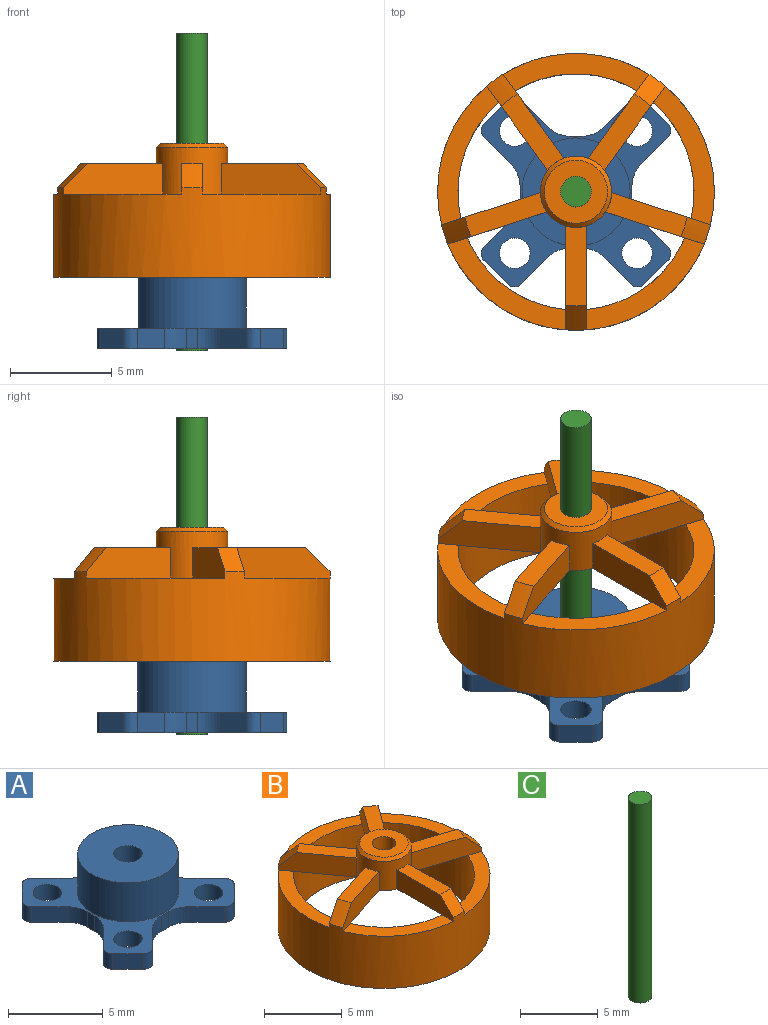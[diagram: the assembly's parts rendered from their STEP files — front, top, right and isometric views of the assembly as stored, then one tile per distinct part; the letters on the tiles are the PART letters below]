
ASSEMBLY  parts=3 mates=2
PART A: 41 faces, bbox 9.3x9.3x3.5 mm
  f0: cylinder r=1.5mm len=1.06mm, axis (0,0,-1), area 1.2mm2, adj f1,f36,f37,f38
  f1: plane 1.33x1.33mm, normal (-0.71,-0.71,0), area 1.9mm2, adj f0,f2,f37,f38
  f2: cylinder r=0.5mm len=1mm, axis (0,0,-1), area 0.8mm2, adj f1,f3,f37,f38
  f3: plane 1.13x1.13mm, normal (0.71,-0.71,0), area 1.6mm2, adj f2,f4,f37,f38
  f4: cylinder r=0.5mm len=1mm, axis (0,0,-1), area 0.8mm2, adj f3,f5,f37,f38
  f5: plane 1.33x1.33mm, normal (0.71,0.71,0), area 1.9mm2, adj f4,f6,f37,f38
  f6: cylinder r=1.5mm len=1.06mm, axis (0,0,-1), area 1.2mm2, adj f5,f7,f37,f38
  f7: plane 1x0.57mm, normal (1,0,0), area 0.6mm2, adj f6,f8,f37,f38
  f8: cylinder r=1.5mm len=1.06mm, axis (0,0,-1), area 1.2mm2, adj f7,f9,f37,f38
  f9: plane 1.33x1.33mm, normal (0.71,-0.71,0), area 1.9mm2, adj f8,f10,f37,f38
  f10: cylinder r=0.5mm len=1mm, axis (0,0,-1), area 0.8mm2, adj f9,f11,f37,f38
  f11: plane 1.13x1.13mm, normal (0.71,0.71,0), area 1.6mm2, adj f10,f12,f37,f38
  f12: cylinder r=0.5mm len=1mm, axis (0,0,-1), area 0.8mm2, adj f11,f13,f37,f38
  f13: plane 1.33x1.33mm, normal (-0.71,0.71,0), area 1.9mm2, adj f12,f14,f37,f38
  f14: cylinder r=1.5mm len=1.06mm, axis (0,0,-1), area 1.2mm2, adj f13,f15,f37,f38
  f15: plane 1x0.57mm, normal (0,1,0), area 0.6mm2, adj f14,f16,f37,f38
  f16: cylinder r=1.5mm len=1.06mm, axis (0,0,-1), area 1.2mm2, adj f15,f17,f37,f38
  f17: plane 1.33x1.33mm, normal (0.71,0.71,0), area 1.9mm2, adj f16,f18,f37,f38
  f18: cylinder r=0.5mm len=1mm, axis (0,0,-1), area 0.8mm2, adj f17,f19,f37,f38
  f19: plane 1.13x1.13mm, normal (-0.71,0.71,0), area 1.6mm2, adj f18,f20,f37,f38
  f20: cylinder r=0.5mm len=1mm, axis (0,0,-1), area 0.8mm2, adj f19,f21,f37,f38
  f21: plane 1.33x1.33mm, normal (-0.71,-0.71,0), area 1.9mm2, adj f20,f22,f37,f38
  f22: cylinder r=1.5mm len=1.06mm, axis (0,0,-1), area 1.2mm2, adj f21,f23,f37,f38
  f23: plane 1x0.57mm, normal (-1,0,0), area 0.6mm2, adj f22,f24,f37,f38
  f24: cylinder r=1.5mm len=1.06mm, axis (0,0,-1), area 1.2mm2, adj f23,f25,f37,f38
  f25: plane 1.33x1.33mm, normal (-0.71,0.71,0), area 1.9mm2, adj f24,f26,f37,f38
  f26: cylinder r=0.5mm len=1mm, axis (0,0,-1), area 0.8mm2, adj f25,f27,f37,f38
  f27: plane 1.13x1.13mm, normal (-0.71,-0.71,0), area 1.6mm2, adj f26,f28,f37,f38
  f28: cylinder r=0.5mm len=1mm, axis (0,0,-1), area 0.8mm2, adj f27,f29,f37,f38
  f29: plane 1.33x1.33mm, normal (0.71,-0.71,0), area 1.9mm2, adj f28,f30,f37,f38
  f30: cylinder r=1.5mm len=1.06mm, axis (0,0,-1), area 1.2mm2, adj f29,f36,f37,f38
  f31: cylinder r=0.75mm len=1.5mm, axis (0,0,-1), area 4.7mm2, adj f37,f38
  f32: cylinder r=0.75mm len=1.5mm, axis (0,0,-1), area 4.7mm2, adj f37,f38
  f33: cylinder r=0.75mm len=1.5mm, axis (0,0,-1), area 4.7mm2, adj f37,f38
  f34: cylinder r=0.75mm len=1.5mm, axis (0,0,-1), area 4.7mm2, adj f37,f38
  f35: cylinder r=0.75mm len=3.5mm, axis (0,0,-1), area 16.5mm2, adj f38,f40
  f36: plane 1x0.57mm, normal (0,-1,0), area 0.6mm2, adj f0,f30,f37,f38
  f37: plane 9.32x9.32mm, normal (0,0,1), area 25.3mm2, adj f0,f1,f2,f3,f4,f5,f6,f7
  f38: plane 9.32x9.32mm, normal (0,0,-1), area 45.7mm2, adj f0,f1,f2,f3,f4,f5,f6,f7
  f39: cylinder r=2.66mm len=5.32mm, axis (0,0,-1), area 41.7mm2, adj f37,f40
  f40: plane 5.32x5.32mm, normal (0,0,1), area 20.4mm2, adj f35,f39
PART B: 33 faces, bbox 13.6x13.6x6.6 mm
  f0: plane 3.74x3.1mm, normal (0,0,1), area 3.9mm2, adj f13,f20,f21,f28
  f1: plane 3.74x3.1mm, normal (0,0,1), area 3.9mm2, adj f12,f13,f22,f29
  f2: plane 4.02x2.16mm, normal (0,0,1), area 3.9mm2, adj f13,f14,f15,f30
  f3: plane 3.92x1mm, normal (0,0,1), area 3.9mm2, adj f13,f16,f17,f26
  f4: plane 6.81x3mm, normal (0,0,1), area 6.9mm2, adj f9,f10,f12,f14
  f5: plane 7.16x1.83mm, normal (0,0,1), area 6.9mm2, adj f9,f10,f21,f22
  f6: plane 6.81x3mm, normal (0,0,1), area 6.9mm2, adj f9,f10,f19,f20
  f7: plane 5.8x4.52mm, normal (0,0,1), area 6.9mm2, adj f9,f10,f17,f18
  f8: plane 5.8x4.52mm, normal (0,0,1), area 6.9mm2, adj f9,f10,f15,f16
  f9: cylinder r=5.8mm len=11.6mm, axis (0,0,-1), area 149.4mm2, adj f4,f5,f6,f7,f8,f11,f25
  f10: cylinder r=6.8mm len=13.6mm, axis (0,0,-1), area 176.7mm2, adj f4,f5,f6,f7,f8,f11,f12,f14
  f11: plane 13.6x13.6mm, normal (0,0,-1), area 39.6mm2, adj f9,f10
  f12: plane 4.14x3.01mm, normal (-0.81,-0.59,0), area 6.9mm2, adj f1,f4,f10,f13,f25,f29
  f13: cylinder r=1.75mm len=3.5mm, axis (0,0,-1), area 17.7mm2, adj f0,f1,f2,f3,f12,f14,f15,f16
  f14: plane 4.86x1.59mm, normal (-0.31,0.95,0), area 6.9mm2, adj f2,f4,f10,f13,f25,f30
  f15: plane 4.86x1.59mm, normal (0.31,-0.95,0), area 6.9mm2, adj f2,f8,f10,f13,f25,f30
  f16: plane 5.11x1.51mm, normal (-1,0,0), area 6.9mm2, adj f3,f8,f10,f13,f25,f26
  f17: plane 5.11x1.51mm, normal (1,0,0), area 6.9mm2, adj f3,f7,f10,f13,f25,f26
  f18: plane 4.86x1.59mm, normal (-0.31,-0.95,0), area 6.9mm2, adj f7,f10,f13,f24,f25,f27
  f19: plane 4.86x1.59mm, normal (0.31,0.95,0), area 6.9mm2, adj f6,f10,f13,f24,f25,f27
  f20: plane 4.14x3.01mm, normal (0.81,-0.59,0), area 6.9mm2, adj f0,f6,f10,f13,f25,f28
  f21: plane 4.14x3.01mm, normal (-0.81,0.59,0), area 6.9mm2, adj f0,f5,f10,f13,f25,f28
  f22: plane 4.14x3.01mm, normal (0.81,0.59,0), area 6.9mm2, adj f1,f5,f10,f13,f25,f29
  f23: cylinder r=0.75mm len=2.5mm, axis (0,0,-1), area 11.8mm2, adj f25,f31
  f24: plane 4.02x2.16mm, normal (0,0,1), area 3.9mm2, adj f13,f18,f19,f27
  f25: plane 11.3x10.77mm, normal (0,0,-1), area 28.2mm2, adj f9,f12,f13,f14,f15,f16,f17,f18
  f26: cone r=5.6mm half-angle=45deg, axis (0,0,-1), area 1.7mm2, adj f3,f10,f16,f17
  f27: cone r=5.6mm half-angle=45deg, axis (0,0,-1), area 1.7mm2, adj f10,f18,f19,f24
  f28: cone r=5.6mm half-angle=45deg, axis (0,0,-1), area 1.7mm2, adj f0,f10,f20,f21
  f29: cone r=5.6mm half-angle=45deg, axis (0,0,-1), area 1.7mm2, adj f1,f10,f12,f22
  f30: cone r=5.6mm half-angle=45deg, axis (0,0,-1), area 1.7mm2, adj f2,f10,f14,f15
  f31: plane 3.1x3.1mm, normal (0,0,1), area 5.8mm2, adj f23,f32
  f32: cone r=1.55mm half-angle=45deg, axis (0,0,-1), area 2.9mm2, adj f13,f31
PART C: 3 faces, bbox 1.5x1.5x15.6 mm
  f0: cylinder r=0.75mm len=15.6mm, axis (0,0,-1), area 73.5mm2, adj f1,f2
  f1: plane 1.5x1.5mm, normal (0,0,1), area 1.8mm2, adj f0
  f2: plane 1.5x1.5mm, normal (0,0,-1), area 1.8mm2, adj f0
PLACE A at identity
PLACE B t=(0,0,3.5)mm
PLACE C t=(0,0,-0.1)mm
MATE fastened B.f23 <-> C.f0  axis (0,0,-1) through (0,0,10.1)mm
MATE fastened C.f0 <-> A.f35  axis (0,0,-1) through (0,0,-0.1)mm
